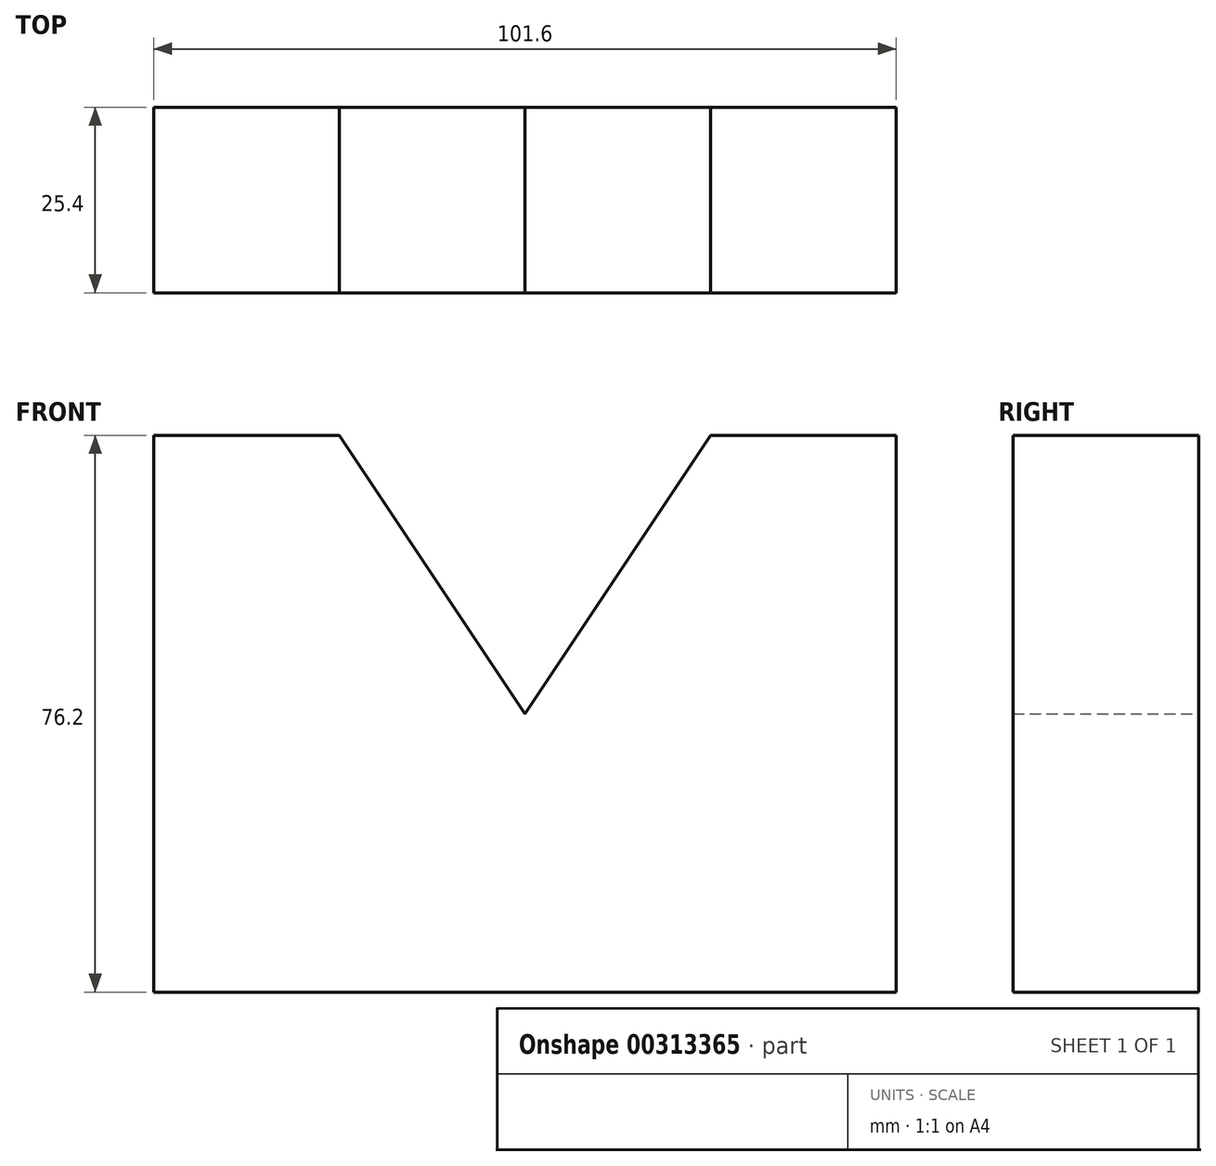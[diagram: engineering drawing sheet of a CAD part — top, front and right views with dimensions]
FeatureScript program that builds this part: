
annotation { "Feature Type Name" : "Feature", "Feature Type Description" : "" }
export const myFeature = defineFeature(function(context is Context, id is Id, definition is map)
    precondition{}
    {
        {
            var Q0;
            Q0=qCreatedBy(makeId("Front.planeOp"),FACE);
            var sketch = newSketch(context, id + "F0", { "sketchPlane" : qUnion([Q0])});
            skLineSegment(sketch, "E0", {"start": v(-50.03, -43.81) * mm, "end": v(51.57, -43.81) * mm});
            skLineSegment(sketch, "E1", {"start": v(51.57, -43.81) * mm, "end": v(51.57, 32.39) * mm});
            skLineSegment(sketch, "E2", {"start": v(51.57, 32.39) * mm, "end": v(26.17, 32.39) * mm});
            skLineSegment(sketch, "E3", {"start": v(-50.03, -43.81) * mm, "end": v(-50.03, 32.39) * mm});
            skLineSegment(sketch, "E4", {"start": v(-50.03, 32.39) * mm, "end": v(-24.63, 32.39) * mm});
            skLineSegment(sketch, "E5", {"start": v(-24.63, 32.39) * mm, "end": v(0.77, -5.71) * mm});
            skLineSegment(sketch, "E6", {"start": v(0.77, -5.71) * mm, "end": v(26.17, 32.39) * mm});
            skSolve(sketch);
        }
        {
            var Q0;
            Q0=makeQuery(id+"F0.imprint","IMPRINT",FACE,{"disambiguationData":[TD([[makeQuery(id+"F0.imprint","IMPRINT",EDGE,{"derivedFrom":sQuery(id+"F0.wireOp",EDGE,"E0")}),1.0]])]});
            extrude(context, id + "F1", {"entities" : qUnion([Q0]), "depth" : 25.4 * mm});
        }
    });
